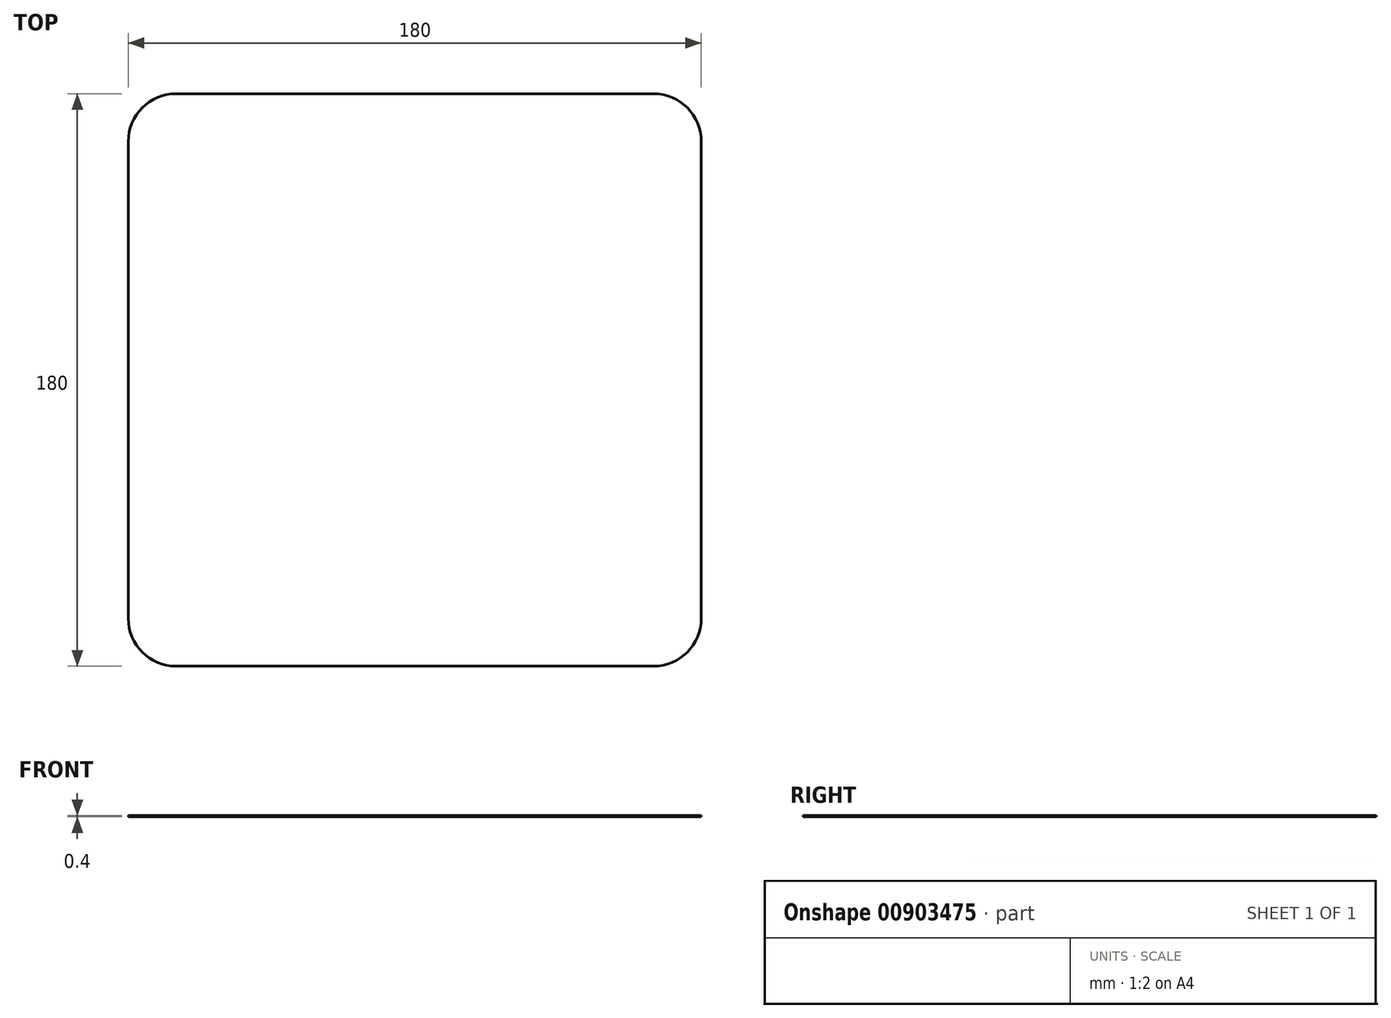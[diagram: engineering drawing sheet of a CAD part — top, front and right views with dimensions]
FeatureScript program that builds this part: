
annotation { "Feature Type Name" : "Feature", "Feature Type Description" : "" }
export const myFeature = defineFeature(function(context is Context, id is Id, definition is map)
    precondition{}
    {
        {
            var Q0;
            Q0=qCreatedBy(makeId("Top.planeOp"), FACE);
            var sketch = newSketch(context, id + "F0", { "sketchPlane" : qUnion([Q0])});
            skLineSegment(sketch, "E0.bottom", {"start": v(75, -90) * mm, "end": v(-75, -90) * mm});
            skLineSegment(sketch, "E0.top", {"start": v(75, 90) * mm, "end": v(-75, 90) * mm});
            skLineSegment(sketch, "E0.left", {"start": v(90, -75) * mm, "end": v(90, 75) * mm});
            skLineSegment(sketch, "E0.right", {"start": v(-90, -75) * mm, "end": v(-90, 75) * mm});
            skPoint(sketch, "E0.middle", {"position": v(0, 0) * mm});
            skPoint(sketch, "E1.visualSharp", {"position": v(-90, 90) * mm});
            skArc(sketch, "E1.filletArc", {"start": v(-75, 90) * mm, "mid": v(-85.6, 85.6) * mm, "end": v(-90, 75) * mm});
            skPoint(sketch, "E2.visualSharp", {"position": v(-90, -90) * mm});
            skArc(sketch, "E2.filletArc", {"start": v(-90, -75) * mm, "mid": v(-85.6, -85.6) * mm, "end": v(-75, -90) * mm});
            skPoint(sketch, "E3.visualSharp", {"position": v(90, -90) * mm});
            skArc(sketch, "E3.filletArc", {"start": v(75, -90) * mm, "mid": v(85.6, -85.6) * mm, "end": v(90, -75) * mm});
            skPoint(sketch, "E4.visualSharp", {"position": v(90, 90) * mm});
            skArc(sketch, "E4.filletArc", {"start": v(90, 75) * mm, "mid": v(85.6, 85.6) * mm, "end": v(75, 90) * mm});
            skSolve(sketch);
        }
        {
            var Q0;
            Q0 = qSketchRegion(id + "F0", true);
            extrude(context, id + "F1", {"entities" : qUnion([Q0]), "domain" : OperationDomain.MODEL, "flatOperationType" : FlatOperationType.REMOVE, "depth" : 0.4 * mm, "offsetDistance" : 25 * mm});
        }
    });
